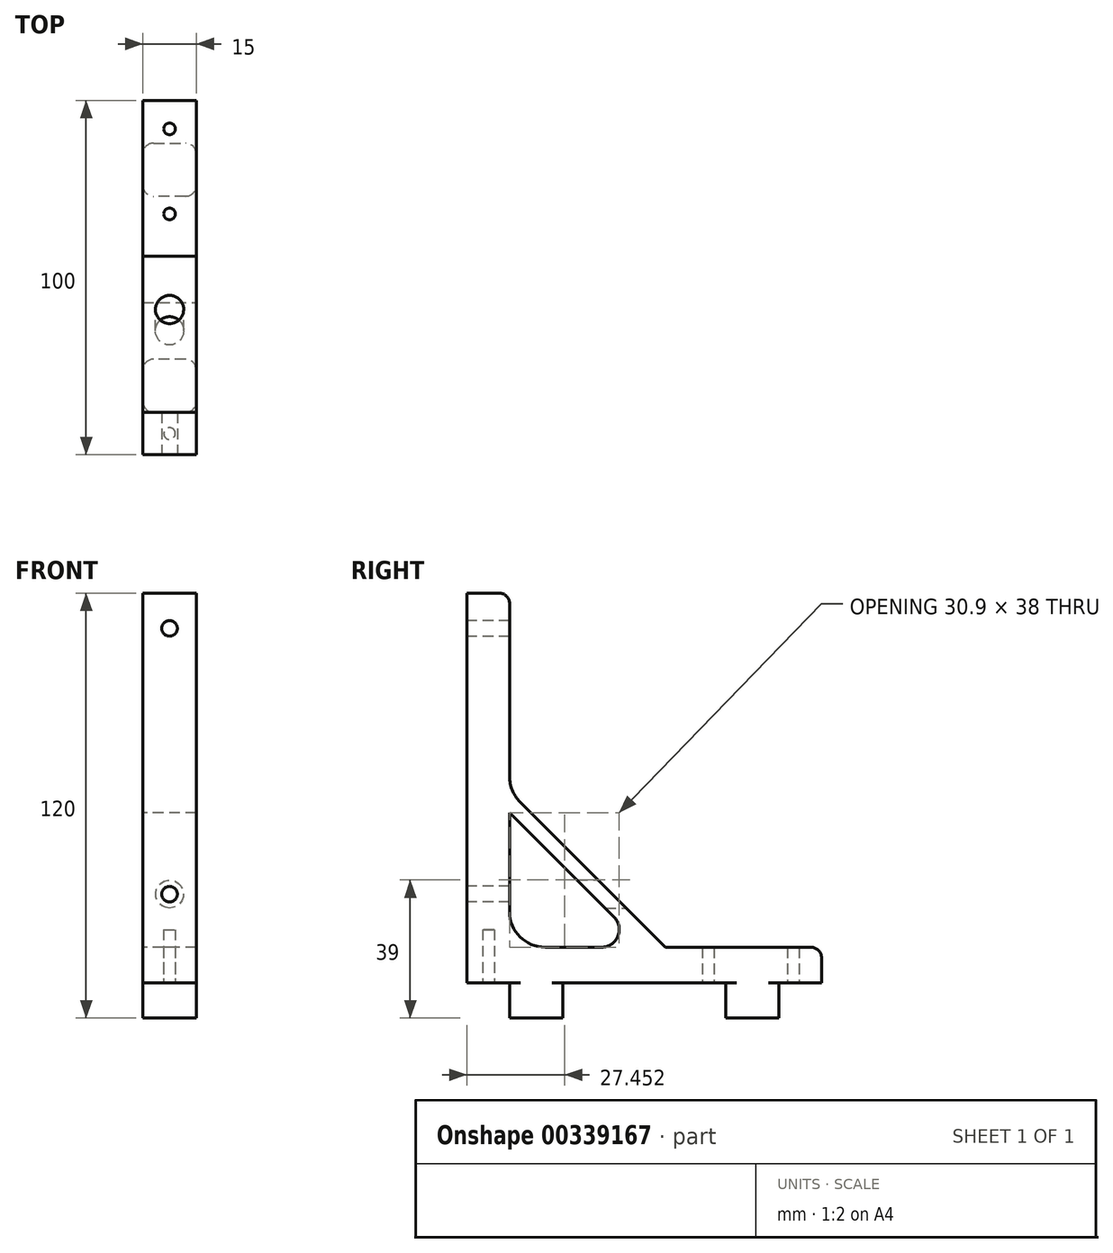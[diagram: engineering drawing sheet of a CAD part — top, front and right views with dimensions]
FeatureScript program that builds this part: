
annotation { "Feature Type Name" : "Feature", "Feature Type Description" : "" }
export const myFeature = defineFeature(function(context is Context, id is Id, definition is map)
    precondition{}
    {
        {
            var Q0;
            Q0=qCreatedBy(makeId("Right.planeOp"),FACE);
            var sketch = newSketch(context, id + "F0", { "sketchPlane" : qUnion([Q0])});
            skLineSegment(sketch, "E0", {"start": v(0, 0) * mm, "end": v(-50, 0) * mm});
            skLineSegment(sketch, "E1", {"start": v(-50, 0) * mm, "end": v(-50, 10) * mm});
            skLineSegment(sketch, "E2", {"start": v(-50, 10) * mm, "end": v(-50, 110) * mm});
            skLineSegment(sketch, "E3", {"start": v(-50, 110) * mm, "end": v(-38, 110) * mm});
            skLineSegment(sketch, "E4", {"start": v(-38, 110) * mm, "end": v(-38, 20) * mm});
            skLineSegment(sketch, "E5", {"start": v(-28, 10) * mm, "end": v(50, 10) * mm});
            skLineSegment(sketch, "E6", {"start": v(50, 10) * mm, "end": v(50, 0) * mm});
            skLineSegment(sketch, "E7", {"start": v(50, 0) * mm, "end": v(0, 0) * mm});
            skPoint(sketch, "E8.visualSharp", {"position": v(-38, 10) * mm});
            skArc(sketch, "E8.filletArc", {"start": v(-38, 20) * mm, "mid": v(-35.07, 12.93) * mm, "end": v(-28, 10) * mm});
            skLineSegment(sketch, "E9", {"start": v(0, 10) * mm, "end": v(-38, 48) * mm});
            skLineSegment(sketch, "E10", {"start": v(-38, 48) * mm, "end": v(-38, 54) * mm});
            skLineSegment(sketch, "E11", {"start": v(-38, 54) * mm, "end": v(6, 10) * mm});
            skLineSegment(sketch, "E12", {"start": v(6, 10) * mm, "end": v(0, 10) * mm});
            skSolve(sketch);
        }
        {
            var Q0;
            Q0=makeQuery(id+"F0.imprint","IMPRINT",FACE,{"disambiguationData":[TD([[makeQuery(id+"F0.imprint","IMPRINT",EDGE,{"derivedFrom":sQuery(id+"F0.wireOp",EDGE,"E0")}),-1.0]])]});
            extrude(context, id + "F1", {"entities" : qUnion([Q0]), "depth" : 15 * mm});
        }
        {
            var Q0;
            Q0=makeQuery(id+"F0.imprint","IMPRINT",FACE,{"disambiguationData":[TD([[makeQuery(id+"F0.imprint","IMPRINT",EDGE,{"derivedFrom":sQuery(id+"F0.wireOp",EDGE,"E9")}),-1.0]])]});
            var Q1;
            Q1=makeQuery(id+"F1.opExtrude","CAP_FACE",FACE,{"disambiguationData":[OSD([sQuery(id+"F0.wireOp",EDGE,"E0"),sQuery(id+"F0.wireOp",EDGE,"E1"),sQuery(id+"F0.wireOp",EDGE,"E2"),sQuery(id+"F0.wireOp",EDGE,"E3"),sQuery(id+"F0.wireOp",EDGE,"E4"),sQuery(id+"F0.wireOp",EDGE,"E5"),sQuery(id+"F0.wireOp",EDGE,"E6"),sQuery(id+"F0.wireOp",EDGE,"E7"),sQuery(id+"F0.wireOp",EDGE,"E8.filletArc"),sQuery(id+"F0.wireOp",EDGE,"E10"),sQuery(id+"F0.wireOp",EDGE,"E12")])],"isStart":false});
            extrude(context, id + "F2", {"entities" : qUnion([Q0]), "operationType" : NewBodyOperationType.ADD, "endBound" : BoundingType.UP_TO_SURFACE, "endBoundEntityFace" : qUnion([Q1]), "depth" : 15.4 * mm});
        }
        {
            var Q0;
            Q0=makeQuery(id+"F2.opExtrude","SWEPT_EDGE",EDGE,{"disambiguationData":[OSD([sQuery(id+"F0.wireOp",EDGE,"E5"),sQuery(id+"F0.wireOp",EDGE,"E11"),sQuery(id+"F0.wireOp",EDGE,"E12")])]});
            var Q1;
            Q1=makeQuery(id+"F2.opExtrude","SWEPT_EDGE",EDGE,{"disambiguationData":[OSD([sQuery(id+"F0.wireOp",EDGE,"E4"),sQuery(id+"F0.wireOp",EDGE,"E10"),sQuery(id+"F0.wireOp",EDGE,"E11")])]});
            fillet(context, id + "F3", {"entities" : qUnion([Q0, Q1]), "radius" : 10 * mm, "tangentPropagation" : true, "allowEdgeOverflow" : false});
        }
        {
            var Q0;
            Q0=makeQuery(id+"F2.opExtrude","SWEPT_EDGE",EDGE,{"disambiguationData":[OSD([sQuery(id+"F0.wireOp",EDGE,"E5"),sQuery(id+"F0.wireOp",EDGE,"E9"),sQuery(id+"F0.wireOp",EDGE,"E12")])]});
            var Q1;
            Q1=makeQuery(id+"F2.opExtrude","SWEPT_EDGE",EDGE,{"disambiguationData":[OSD([sQuery(id+"F0.wireOp",EDGE,"E4"),sQuery(id+"F0.wireOp",EDGE,"E9"),sQuery(id+"F0.wireOp",EDGE,"E10")])]});
            fillet(context, id + "F4", {"entities" : qUnion([Q0, Q1]), "radius" : 5 * mm, "tangentPropagation" : true, "allowEdgeOverflow" : false});
        }
        {
            var Q0;
            Q0=makeQuery(id+"F1.opExtrude","SWEPT_EDGE",EDGE,{"disambiguationData":[OSD([sQuery(id+"F0.wireOp",EDGE,"E5"),sQuery(id+"F0.wireOp",EDGE,"E6")])]});
            var Q1;
            Q1=makeQuery(id+"F1.opExtrude","SWEPT_EDGE",EDGE,{"disambiguationData":[OSD([sQuery(id+"F0.wireOp",EDGE,"E3"),sQuery(id+"F0.wireOp",EDGE,"E4")])]});
            fillet(context, id + "F5", {"entities" : qUnion([Q0, Q1]), "radius" : 3 * mm, "tangentPropagation" : true, "allowEdgeOverflow" : false});
        }
        {
            var Q0;
            Q0=makeQuery(id+"F1.opExtrude","SWEPT_FACE",FACE,{"disambiguationData":[OSD([sQuery(id+"F0.wireOp",EDGE,"E1"),sQuery(id+"F0.wireOp",EDGE,"E2")])]});
            var sketch = newSketch(context, id + "F6", { "sketchPlane" : qUnion([Q0])});
            skLineSegment(sketch, "E13", {"start": v(7.5, -20.48) * mm, "end": v(7.5, 209.61) * mm, "construction": true});
            skLineSegment(sketch, "E14", {"start": v(-37.7, 100) * mm, "end": v(54.54, 100) * mm, "construction": true});
            skLineSegment(sketch, "E15", {"start": v(-26.5, 25) * mm, "end": v(44.92, 25) * mm, "construction": true});
            skPoint(sketch, "E16", {"position": v(7.5, 100) * mm});
            skPoint(sketch, "E17", {"position": v(7.5, 25) * mm});
            skSolve(sketch);
        }
        {
            var Q0;
            Q0=sQuery(id+"F6.wireOp",VERTEX,"E16");
            var Q1;
            Q1=sQuery(id+"F6.wireOp",VERTEX,"E17");
            var Q2;
            Q2=makeQuery(id+"F1.opExtrude","SWEPT_BODY",BODY,{"disambiguationData":[OSD([sQuery(id+"F0.wireOp",EDGE,"E0"),sQuery(id+"F0.wireOp",EDGE,"E1"),sQuery(id+"F0.wireOp",EDGE,"E2"),sQuery(id+"F0.wireOp",EDGE,"E3"),sQuery(id+"F0.wireOp",EDGE,"E4"),sQuery(id+"F0.wireOp",EDGE,"E5"),sQuery(id+"F0.wireOp",EDGE,"E6"),sQuery(id+"F0.wireOp",EDGE,"E7"),sQuery(id+"F0.wireOp",EDGE,"E8.filletArc"),sQuery(id+"F0.wireOp",EDGE,"E10"),sQuery(id+"F0.wireOp",EDGE,"E12")])]});
            hole(context, id + "F7", {"style" : HoleStyle.SIMPLE, "endStyle" : HoleEndStyle.THROUGH, "standardTappedOrClearance" : lookupTablePath({ "standard" : "ISO", "fit" : "Normal", "size" : "M4", "type" : "Clearance" }), "standardBlindInLast" : lookupTablePath({ "fit" : "Standard", "standard" : "ISO", "size" : "M4", "type" : "Clearance" }), "holeDiameter" : 4.4 * mm, "tappedDepth" : 12 * mm, "tapClearance" : 3, "locations" : qUnion([Q0, Q1]), "scope" : qUnion([Q2])});
        }
        {
            var Q0;
            Q0=qCreatedBy(makeId("Front.planeOp"),FACE);
            var sketch = newSketch(context, id + "F8", { "sketchPlane" : qUnion([Q0])});
            skCircle(sketch, "E18", {"center": v(7.5, 25) * mm, "radius": 4 * mm});
            skSolve(sketch);
        }
        {
            var Q0;
            Q0=makeQuery(id+"F8.imprint","IMPRINT",FACE,{"disambiguationData":[TD([[makeQuery(id+"F8.imprint","IMPRINT",EDGE,{"derivedFrom":sQuery(id+"F8.wireOp",EDGE,"E18")}),1.0]])]});
            extrude(context, id + "F9", {"entities" : qUnion([Q0]), "operationType" : NewBodyOperationType.REMOVE, "depth" : 23.5 * mm});
        }
        {
            var Q0;
            Q0=makeQuery(id+"F1.opExtrude","SWEPT_FACE",FACE,{"disambiguationData":[OSD([sQuery(id+"F0.wireOp",EDGE,"E0"),sQuery(id+"F0.wireOp",EDGE,"E7")])]});
            var sketch = newSketch(context, id + "F10", { "sketchPlane" : qUnion([Q0])});
            skLineSegment(sketch, "E19", {"start": v(7.5, 55.23) * mm, "end": v(7.5, -72.79) * mm, "construction": true});
            skCircle(sketch, "E20", {"center": v(7.5, 44) * mm, "radius": 1.65 * mm});
            skCircle(sketch, "E21", {"center": v(7.5, -42) * mm, "radius": 1.65 * mm});
            skCircle(sketch, "E22", {"center": v(7.5, -18) * mm, "radius": 1.65 * mm});
            skLineSegment(sketch, "E23", {"start": v(0, -38) * mm, "end": v(15, -38) * mm});
            skLineSegment(sketch, "E24", {"start": v(15, -38) * mm, "end": v(15, -23) * mm});
            skLineSegment(sketch, "E25", {"start": v(15, -23) * mm, "end": v(0, -23) * mm});
            skLineSegment(sketch, "E26", {"start": v(0, -23) * mm, "end": v(0, -38) * mm});
            skLineSegment(sketch, "E27", {"start": v(0, 38) * mm, "end": v(15, 38) * mm});
            skLineSegment(sketch, "E28", {"start": v(15, 38) * mm, "end": v(15, 23) * mm});
            skLineSegment(sketch, "E29", {"start": v(15, 23) * mm, "end": v(0, 23) * mm});
            skLineSegment(sketch, "E30", {"start": v(0, 23) * mm, "end": v(0, 38) * mm});
            skSolve(sketch);
        }
        {
            var Q0;
            {var subQ0=sQuery(id+"F10.wireOp",EDGE,"E27");Q0=makeQuery(id+"F10.imprint","IMPRINT",FACE,{"disambiguationData":[TD([[makeQuery(id+"F10.imprint","IMPRINT",EDGE,{"derivedFrom":subQ0}),-1.0]])]});}
            extrude(context, id + "F11", {"entities" : qUnion([Q0]), "operationType" : NewBodyOperationType.ADD, "depth" : 10 * mm});
        }
        {
            var Q0;
            Q0=makeQuery(id+"F10.imprint","IMPRINT",FACE,{"disambiguationData":[TD([[makeQuery(id+"F10.imprint","IMPRINT",EDGE,{"derivedFrom":sQuery(id+"F10.wireOp",EDGE,"E23")}),1.0]])]});
            extrude(context, id + "F12", {"entities" : qUnion([Q0]), "operationType" : NewBodyOperationType.ADD, "depth" : 10 * mm});
        }
        {
            var Q0;
            Q0=makeQuery(id+"F10.imprint","IMPRINT",FACE,{"disambiguationData":[TD([[makeQuery(id+"F10.imprint","IMPRINT",EDGE,{"derivedFrom":sQuery(id+"F10.wireOp",EDGE,"E21")}),1.0]])]});
            var Q1;
            Q1=makeQuery(id+"F10.imprint","IMPRINT",FACE,{"disambiguationData":[TD([[makeQuery(id+"F10.imprint","IMPRINT",EDGE,{"derivedFrom":sQuery(id+"F10.wireOp",EDGE,"E22")}),1.0]])]});
            var Q2;
            Q2=makeQuery(id+"F10.imprint","IMPRINT",FACE,{"disambiguationData":[TD([[makeQuery(id+"F10.imprint","IMPRINT",EDGE,{"derivedFrom":sQuery(id+"F10.wireOp",EDGE,"E20")}),1.0]])]});
            var Q3;
            Q3=sQuery(id+"F10.wireOp",EDGE,"E22");
            var Q4;
            Q4=sQuery(id+"F10.wireOp",EDGE,"E20");
            var Q5;
            Q5=sQuery(id+"F10.wireOp",EDGE,"E21");
            extrude(context, id + "F13", {"entities" : qUnion([Q0, Q1, Q2]), "operationType" : NewBodyOperationType.REMOVE, "surfaceEntities" : qUnion([Q3, Q4, Q5]), "oppositeDirection" : true, "depth" : 15 * mm});
        }
        {
            var Q0;
            Q0=makeQuery(id+"F11.opExtrude","SWEPT_EDGE",EDGE,{"disambiguationData":[OSD([sQuery(id+"F0.wireOp",EDGE,"E0"),sQuery(id+"F0.wireOp",EDGE,"E7"),sQuery(id+"F10.wireOp",EDGE,"E27"),sQuery(id+"F10.wireOp",EDGE,"E28")])]});
            var Q1;
            Q1=makeQuery(id+"F11.opExtrude","SWEPT_EDGE",EDGE,{"disambiguationData":[OSD([sQuery(id+"F0.wireOp",EDGE,"E0"),sQuery(id+"F0.wireOp",EDGE,"E7"),sQuery(id+"F10.wireOp",EDGE,"E27"),sQuery(id+"F10.wireOp",EDGE,"E30")])]});
            var Q2;
            Q2=makeQuery(id+"F11.opExtrude","SWEPT_EDGE",EDGE,{"disambiguationData":[OSD([sQuery(id+"F0.wireOp",EDGE,"E0"),sQuery(id+"F0.wireOp",EDGE,"E7"),sQuery(id+"F10.wireOp",EDGE,"E29")])]});
            var Q3;
            Q3=makeQuery(id+"F11.opExtrude","SWEPT_EDGE",EDGE,{"disambiguationData":[OSD([sQuery(id+"F0.wireOp",EDGE,"E0"),sQuery(id+"F0.wireOp",EDGE,"E7"),sQuery(id+"F10.wireOp",EDGE,"E29"),sQuery(id+"F10.wireOp",EDGE,"E30")])]});
            var Q4;
            Q4=makeQuery(id+"F12.opExtrude","SWEPT_EDGE",EDGE,{"disambiguationData":[OSD([sQuery(id+"F0.wireOp",EDGE,"E0"),sQuery(id+"F0.wireOp",EDGE,"E7"),sQuery(id+"F10.wireOp",EDGE,"E24"),sQuery(id+"F10.wireOp",EDGE,"E25")])]});
            var Q5;
            Q5=makeQuery(id+"F12.opExtrude","SWEPT_EDGE",EDGE,{"disambiguationData":[OSD([sQuery(id+"F0.wireOp",EDGE,"E0"),sQuery(id+"F0.wireOp",EDGE,"E7"),sQuery(id+"F10.wireOp",EDGE,"E23"),sQuery(id+"F10.wireOp",EDGE,"E24")])]});
            var Q6;
            Q6=makeQuery(id+"F12.opExtrude","SWEPT_EDGE",EDGE,{"disambiguationData":[OSD([sQuery(id+"F0.wireOp",EDGE,"E0"),sQuery(id+"F0.wireOp",EDGE,"E7"),sQuery(id+"F10.wireOp",EDGE,"E23"),sQuery(id+"F10.wireOp",EDGE,"E26")])]});
            var Q7;
            Q7=makeQuery(id+"F12.opExtrude","SWEPT_EDGE",EDGE,{"disambiguationData":[OSD([sQuery(id+"F0.wireOp",EDGE,"E0"),sQuery(id+"F0.wireOp",EDGE,"E7"),sQuery(id+"F10.wireOp",EDGE,"E25"),sQuery(id+"F10.wireOp",EDGE,"E26")])]});
            fillet(context, id + "F14", {"entities" : qUnion([Q0, Q1, Q2, Q3, Q4, Q5, Q6, Q7]), "radius" : 3 * mm, "tangentPropagation" : true, "allowEdgeOverflow" : false});
        }
    });
